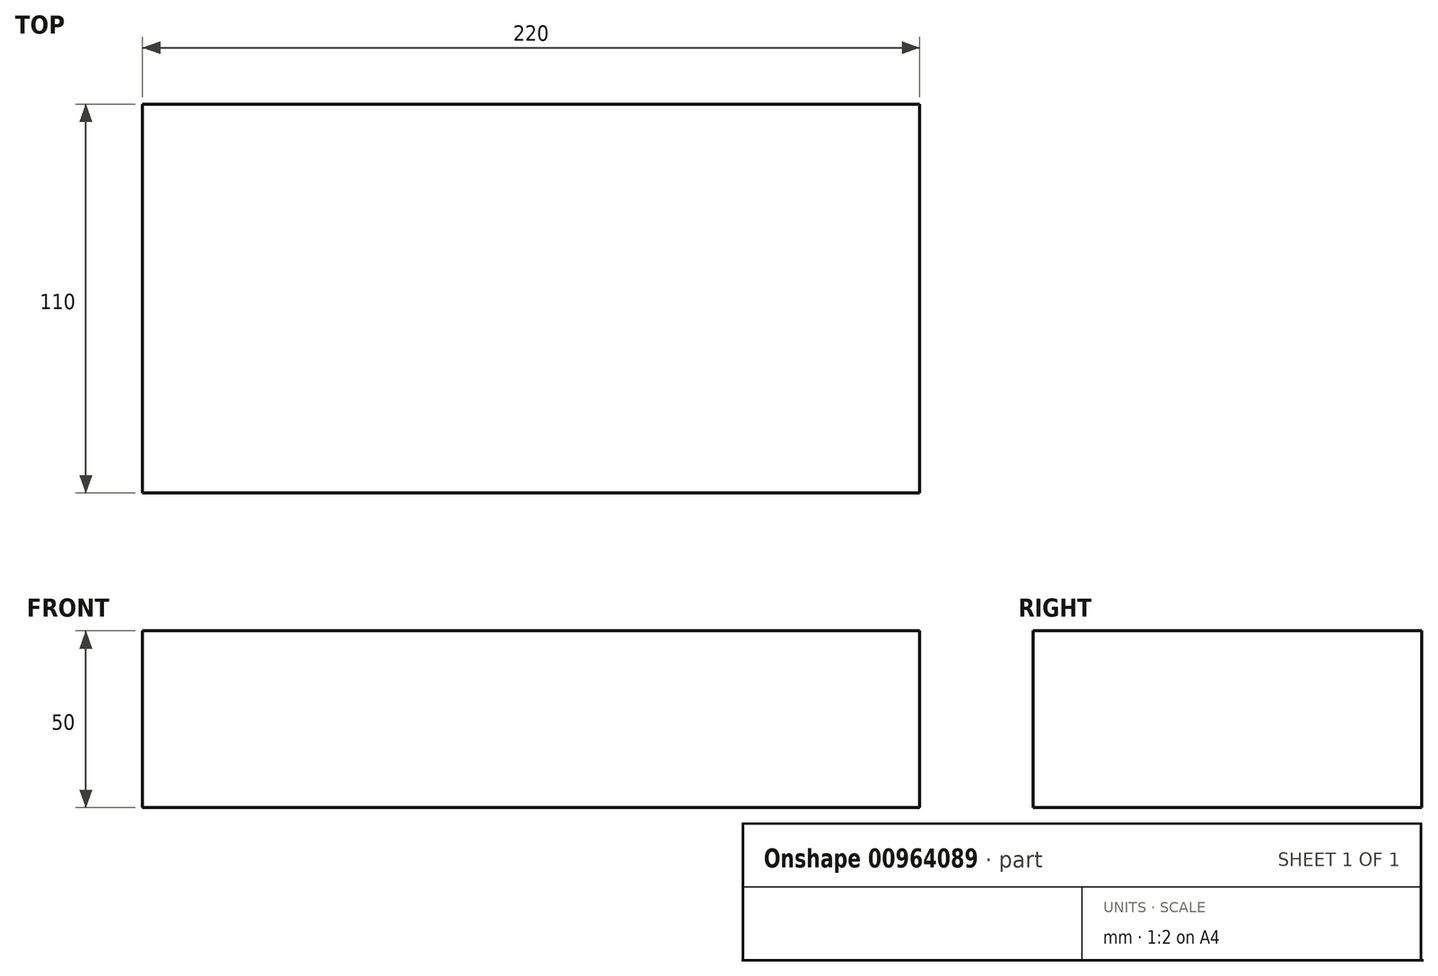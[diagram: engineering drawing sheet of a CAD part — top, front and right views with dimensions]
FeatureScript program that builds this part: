
annotation { "Feature Type Name" : "Feature", "Feature Type Description" : "" }
export const myFeature = defineFeature(function(context is Context, id is Id, definition is map)
    precondition{}
    {
        {
            var Q0;
            Q0=qCreatedBy(makeId("Top.planeOp"),FACE);
            var sketch = newSketch(context, id + "F0", { "sketchPlane" : qUnion([Q0])});
            skLineSegment(sketch, "E0.bottom", {"start": v(-128.57, 39.4) * mm, "end": v(91.43, 39.4) * mm});
            skLineSegment(sketch, "E0.top", {"start": v(-128.57, -70.6) * mm, "end": v(91.43, -70.6) * mm});
            skLineSegment(sketch, "E0.left", {"start": v(-128.57, 39.4) * mm, "end": v(-128.57, -70.6) * mm});
            skLineSegment(sketch, "E0.right", {"start": v(91.43, 39.4) * mm, "end": v(91.43, -70.6) * mm});
            skSolve(sketch);
        }
        {
            var Q0;
            Q0 = qSketchRegion(id + "F0", true);
            extrude(context, id + "F1", {"entities" : qUnion([Q0]), "depth" : 50 * mm, "offsetDistance" : 25 * mm});
        }
    });
